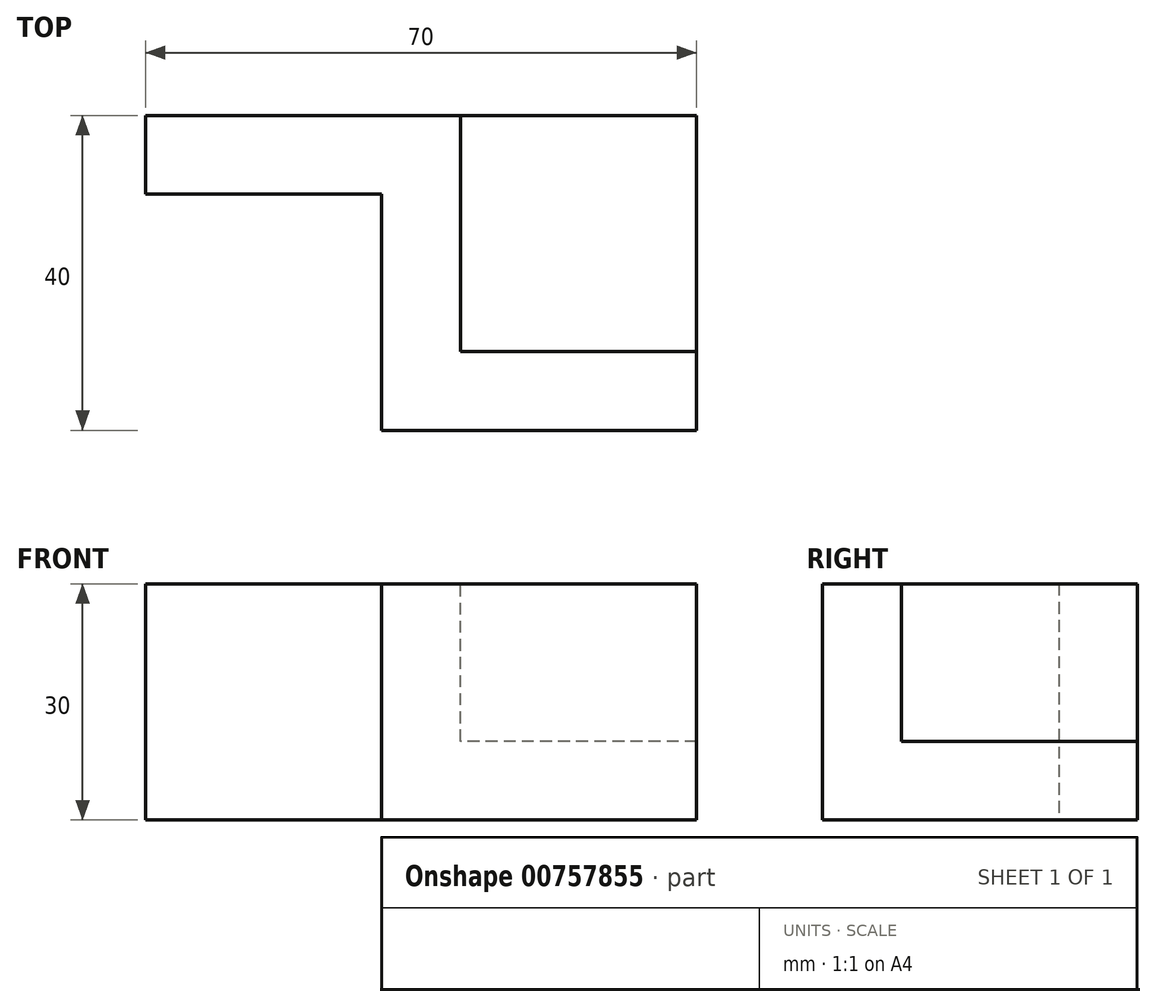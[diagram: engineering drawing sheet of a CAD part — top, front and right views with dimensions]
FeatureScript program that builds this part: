
annotation { "Feature Type Name" : "Feature", "Feature Type Description" : "" }
export const myFeature = defineFeature(function(context is Context, id is Id, definition is map)
    precondition{}
    {
        {
            var Q0;
            Q0=qCreatedBy(makeId("Top.planeOp"),FACE);
            var sketch = newSketch(context, id + "F0", { "sketchPlane" : qUnion([Q0])});
            skLineSegment(sketch, "E0", {"start": v(0, 0) * mm, "end": v(40, 0) * mm});
            skLineSegment(sketch, "E1", {"start": v(40, 0) * mm, "end": v(40, 40) * mm});
            skLineSegment(sketch, "E2", {"start": v(40, 40) * mm, "end": v(-30, 40) * mm});
            skLineSegment(sketch, "E3", {"start": v(-30, 40) * mm, "end": v(-30, 30) * mm});
            skLineSegment(sketch, "E4", {"start": v(-30, 30) * mm, "end": v(0, 30) * mm});
            skLineSegment(sketch, "E5", {"start": v(0, 30) * mm, "end": v(0, 0) * mm});
            skSolve(sketch);
        }
        {
            var Q0;
            Q0 = qSketchRegion(id + "F0", true);
            extrude(context, id + "F1", {"entities" : qUnion([Q0]), "depth" : 30 * mm, "offsetDistance" : 25 * mm});
        }
        {
            var Q0;
            Q0=makeQuery(id+"F1.opExtrude","CAP_FACE",FACE,{"disambiguationData":[OSD([sQuery(id+"F0.wireOp",EDGE,"E0"),sQuery(id+"F0.wireOp",EDGE,"E1"),sQuery(id+"F0.wireOp",EDGE,"E2"),sQuery(id+"F0.wireOp",EDGE,"E3"),sQuery(id+"F0.wireOp",EDGE,"E4"),sQuery(id+"F0.wireOp",EDGE,"E5")])],"isStart":false});
            var sketch = newSketch(context, id + "F2", { "sketchPlane" : qUnion([Q0])});
            skLineSegment(sketch, "E6", {"start": v(40, 40) * mm, "end": v(10, 40) * mm});
            skLineSegment(sketch, "E7", {"start": v(10, 40) * mm, "end": v(10, 10) * mm});
            skLineSegment(sketch, "E8", {"start": v(10, 10) * mm, "end": v(40, 10) * mm});
            skLineSegment(sketch, "E9", {"start": v(40, 10) * mm, "end": v(40, 40) * mm});
            skSolve(sketch);
        }
        {
            var Q0;
            Q0 = qSketchRegion(id + "F2", true);
            extrude(context, id + "F3", {"entities" : qUnion([Q0]), "operationType" : NewBodyOperationType.REMOVE, "oppositeDirection" : true, "depth" : 20 * mm, "offsetDistance" : 25 * mm});
        }
    });
